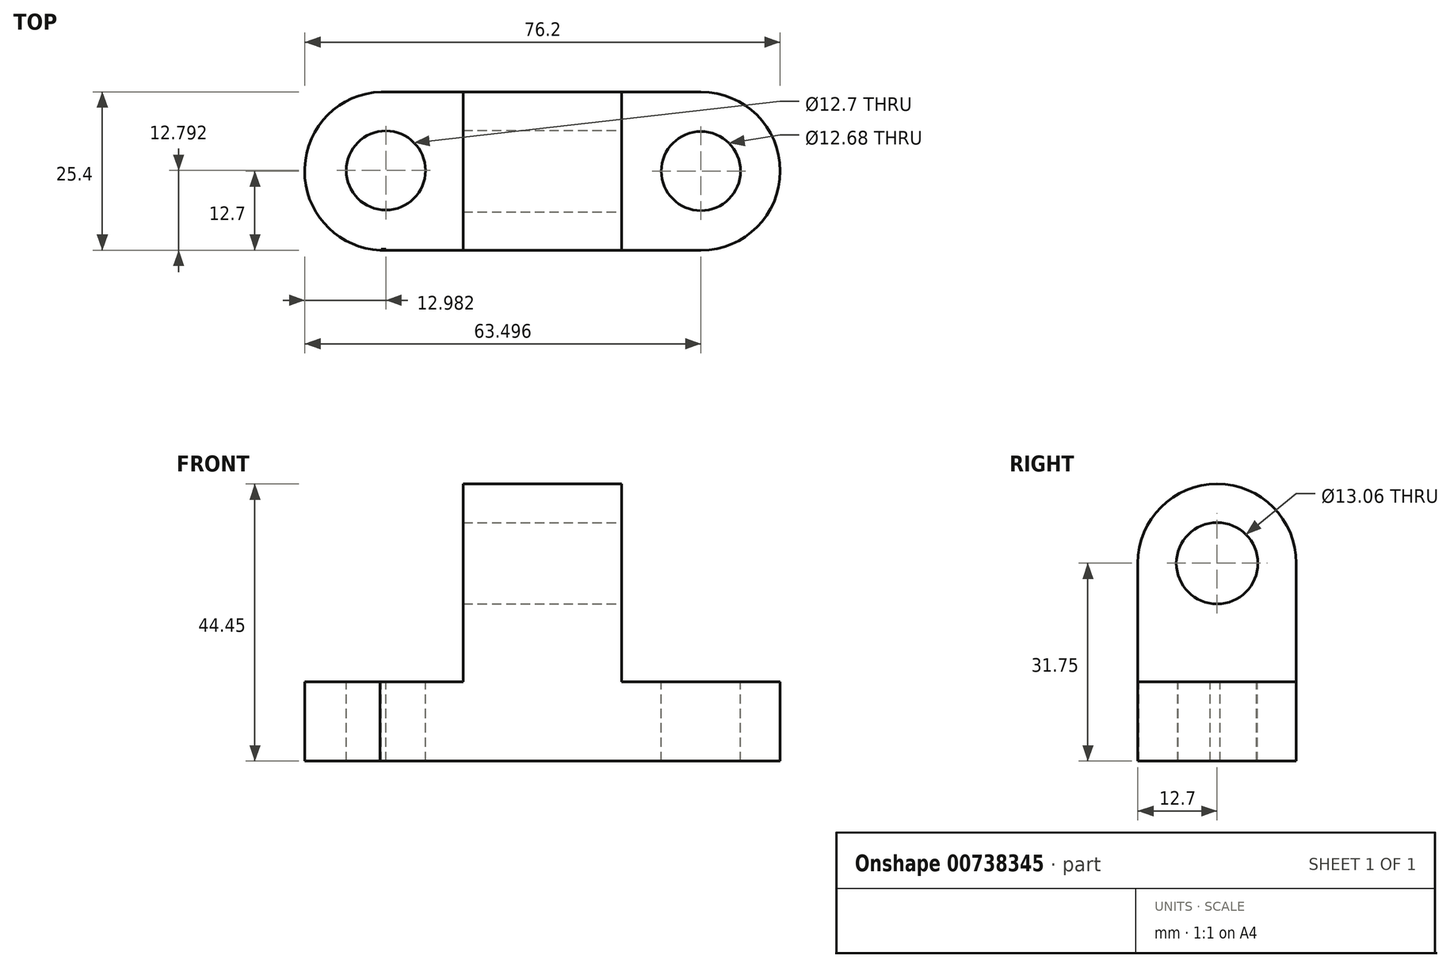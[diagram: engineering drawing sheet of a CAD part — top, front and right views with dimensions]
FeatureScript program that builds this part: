
annotation { "Feature Type Name" : "Feature", "Feature Type Description" : "" }
export const myFeature = defineFeature(function(context is Context, id is Id, definition is map)
    precondition{}
    {
        {
            var Q0;
            Q0=qCreatedBy(makeId("Front.planeOp"),FACE);
            var sketch = newSketch(context, id + "F0", { "sketchPlane" : qUnion([Q0])});
            skLineSegment(sketch, "E0", {"start": v(-38.15, 0) * mm, "end": v(38.05, 0) * mm});
            skLineSegment(sketch, "E1", {"start": v(38.05, 0) * mm, "end": v(38.05, 12.7) * mm});
            skLineSegment(sketch, "E2", {"start": v(38.05, 12.7) * mm, "end": v(12.65, 12.7) * mm});
            skLineSegment(sketch, "E3", {"start": v(12.65, 12.7) * mm, "end": v(12.65, 44.45) * mm});
            skLineSegment(sketch, "E4", {"start": v(12.65, 44.45) * mm, "end": v(-12.75, 44.45) * mm});
            skLineSegment(sketch, "E5", {"start": v(-12.75, 44.45) * mm, "end": v(-12.75, 12.7) * mm});
            skLineSegment(sketch, "E6", {"start": v(-38.15, 0) * mm, "end": v(-38.15, 12.7) * mm});
            skLineSegment(sketch, "E7", {"start": v(-38.15, 12.7) * mm, "end": v(-12.75, 12.7) * mm});
            skSolve(sketch);
        }
        {
            var Q0;
            Q0 = qSketchRegion(id + "F0", true);
            extrude(context, id + "F1", {"entities" : qUnion([Q0]), "depth" : 25.4 * mm, "offsetDistance" : 25.4 * mm});
        }
        {
            var Q0;
            Q0=makeQuery(id+"F1.opExtrude","SWEPT_FACE",FACE,{"disambiguationData":[OSD([sQuery(id+"F0.wireOp",EDGE,"E3")])]});
            var sketch = newSketch(context, id + "F2", { "sketchPlane" : qUnion([Q0])});
            skLineSegment(sketch, "E8", {"start": v(-25.4, 31.75) * mm, "end": v(0, 31.75) * mm});
            skLineSegment(sketch, "E9", {"start": v(0, 31.75) * mm, "end": v(0, 44.45) * mm});
            skArc(sketch, "E10", {"start": v(0, 31.75) * mm, "mid": v(-12.7, 44.45) * mm, "end": v(-25.4, 31.75) * mm});
            skCircle(sketch, "E11", {"center": v(-12.7, 31.75) * mm, "radius": 6.53 * mm});
            skSolve(sketch);
        }
        {
            var Q0;
            {var subQ0=sQuery(id+"F2.wireOp",EDGE,"E11");var subQ1=sQuery(id+"F2.wireOp",EDGE,"E8");var subQ2=makeQuery(id+"F2.imprint","INTERSECT",VERTEX,{"disambiguationData":[OD(0.0)],"derivedFrom":[subQ1,subQ0]});Q0=makeQuery(id+"F2.imprint","IMPRINT",FACE,{"disambiguationData":[TD([[makeQuery(id+"F2.imprint","IMPRINT",EDGE,{"disambiguationData":[TD([[subQ2,-1.0]])],"derivedFrom":subQ1}),1.0]])]});}
            var Q1;
            {var subQ0=sQuery(id+"F2.wireOp",EDGE,"E11");var subQ1=sQuery(id+"F2.wireOp",EDGE,"E8");var subQ2=makeQuery(id+"F2.imprint","INTERSECT",VERTEX,{"disambiguationData":[OD(0.0)],"derivedFrom":[subQ1,subQ0]});Q1=makeQuery(id+"F2.imprint","IMPRINT",FACE,{"disambiguationData":[TD([[makeQuery(id+"F2.imprint","IMPRINT",EDGE,{"disambiguationData":[TD([[subQ2,-1.0]])],"derivedFrom":subQ1}),-1.0]])]});}
            var Q2;
            {var subQ0=sQuery(id+"F2.wireOp",EDGE,"E10");var subQ1=sQuery(id+"F0.wireOp",EDGE,"E3");var subQ2=makeQuery(id+"F1.opExtrude","CAP_EDGE",EDGE,{"disambiguationData":[OSD([subQ1])],"isStart":false});var subQ3=makeQuery(id+"F2.imprint","INTERSECT",VERTEX,{"derivedFrom":[subQ2,sQuery(id+"F2.wireOp",EDGE,"E8"),subQ0]});Q2=makeQuery(id+"F2.imprint","IMPRINT",FACE,{"disambiguationData":[TD([[makeQuery(id+"F2.imprint","IMPRINT",EDGE,{"disambiguationData":[TD([[subQ3,1.0]])],"derivedFrom":subQ0}),-1.0]])]});}
            var Q3;
            {var subQ0=sQuery(id+"F2.wireOp",EDGE,"E9");Q3=makeQuery(id+"F2.imprint","IMPRINT",FACE,{"disambiguationData":[TD([[makeQuery(id+"F2.imprint","IMPRINT",EDGE,{"derivedFrom":subQ0}),1.0]])]});}
            extrude(context, id + "F3", {"entities" : qUnion([Q0, Q1, Q2, Q3]), "operationType" : NewBodyOperationType.REMOVE, "endBound" : BoundingType.THROUGH_ALL, "oppositeDirection" : true, "depth" : 25.4 * mm, "offsetDistance" : 25.4 * mm});
        }
        {
            var Q0;
            Q0=makeQuery(id+"F1.opExtrude","SWEPT_FACE",FACE,{"disambiguationData":[OSD([sQuery(id+"F0.wireOp",EDGE,"E2")])]});
            var sketch = newSketch(context, id + "F4", { "sketchPlane" : qUnion([Q0])});
            skLineSegment(sketch, "E12", {"start": v(25.35, -25.4) * mm, "end": v(25.35, 0) * mm});
            skLineSegment(sketch, "E13", {"start": v(25.35, 0) * mm, "end": v(38.05, 0) * mm});
            skArc(sketch, "E14", {"start": v(25.35, -25.4) * mm, "mid": v(38.05, -12.7) * mm, "end": v(25.35, 0) * mm});
            skLineSegment(sketch, "E15", {"start": v(-25.17, 0) * mm, "end": v(-25.17, -25.22) * mm});
            skLineSegment(sketch, "E16", {"start": v(-25.17, -25.22) * mm, "end": v(-37.87, -25.22) * mm});
            skCircle(sketch, "E17", {"center": v(-25.17, -12.6) * mm, "radius": 6.35 * mm});
            skCircle(sketch, "E18", {"center": v(25.35, -12.7) * mm, "radius": 6.34 * mm});
            skArc(sketch, "E19", {"start": v(-25.17, 0) * mm, "mid": v(-38.16, -12.6) * mm, "end": v(-25.17, -25.22) * mm});
            skSolve(sketch);
        }
        {
            var Q0;
            {var subQ0=sQuery(id+"F4.wireOp",EDGE,"E19");var subQ1=sQuery(id+"F4.wireOp",EDGE,"E16");var subQ3=makeQuery(id+"F4.imprint","INTERSECT",VERTEX,{"derivedFrom":[subQ1,subQ0]});Q0=makeQuery(id+"F4.imprint","IMPRINT",FACE,{"disambiguationData":[TD([[makeQuery(id+"F4.imprint","IMPRINT",EDGE,{"disambiguationData":[TD([[subQ3,1.0]])],"derivedFrom":subQ1}),1.0]])]});}
            var Q1;
            {var subQ0=sQuery(id+"F4.wireOp",EDGE,"E18");var subQ1=sQuery(id+"F4.wireOp",EDGE,"E12");var subQ2=makeQuery(id+"F4.imprint","INTERSECT",VERTEX,{"disambiguationData":[OD(0.0)],"derivedFrom":[subQ1,subQ0]});Q1=makeQuery(id+"F4.imprint","IMPRINT",FACE,{"disambiguationData":[TD([[makeQuery(id+"F4.imprint","IMPRINT",EDGE,{"disambiguationData":[TD([[subQ2,-1.0]])],"derivedFrom":subQ1}),1.0]])]});}
            var Q2;
            {var subQ0=sQuery(id+"F4.wireOp",EDGE,"E18");var subQ1=sQuery(id+"F4.wireOp",EDGE,"E12");var subQ2=makeQuery(id+"F4.imprint","INTERSECT",VERTEX,{"disambiguationData":[OD(0.0)],"derivedFrom":[subQ1,subQ0]});Q2=makeQuery(id+"F4.imprint","IMPRINT",FACE,{"disambiguationData":[TD([[makeQuery(id+"F4.imprint","IMPRINT",EDGE,{"disambiguationData":[TD([[subQ2,-1.0]])],"derivedFrom":subQ1}),-1.0]])]});}
            var Q3;
            {var subQ0=sQuery(id+"F4.wireOp",EDGE,"E17");var subQ1=sQuery(id+"F4.wireOp",EDGE,"E15");var subQ2=makeQuery(id+"F4.imprint","INTERSECT",VERTEX,{"disambiguationData":[OD(0.0)],"derivedFrom":[subQ1,subQ0]});Q3=makeQuery(id+"F4.imprint","IMPRINT",FACE,{"disambiguationData":[TD([[makeQuery(id+"F4.imprint","IMPRINT",EDGE,{"disambiguationData":[TD([[subQ2,-1.0]])],"derivedFrom":subQ1}),-1.0]])]});}
            var Q4;
            {var subQ0=sQuery(id+"F4.wireOp",EDGE,"E17");var subQ1=sQuery(id+"F4.wireOp",EDGE,"E15");var subQ2=makeQuery(id+"F4.imprint","INTERSECT",VERTEX,{"disambiguationData":[OD(0.0)],"derivedFrom":[subQ1,subQ0]});Q4=makeQuery(id+"F4.imprint","IMPRINT",FACE,{"disambiguationData":[TD([[makeQuery(id+"F4.imprint","IMPRINT",EDGE,{"disambiguationData":[TD([[subQ2,-1.0]])],"derivedFrom":subQ1}),1.0]])]});}
            var Q5;
            {var subQ0=sQuery(id+"F4.wireOp",EDGE,"E13");Q5=makeQuery(id+"F4.imprint","IMPRINT",FACE,{"disambiguationData":[TD([[makeQuery(id+"F4.imprint","IMPRINT",EDGE,{"derivedFrom":subQ0}),1.0]])]});}
            var Q6;
            {var subQ0=sQuery(id+"F4.wireOp",EDGE,"E14");var subQ1=sQuery(id+"F0.wireOp",EDGE,"E2");var subQ2=makeQuery(id+"F1.opExtrude","CAP_EDGE",EDGE,{"disambiguationData":[OSD([subQ1])],"isStart":false});var subQ3=makeQuery(id+"F4.imprint","INTERSECT",VERTEX,{"derivedFrom":[subQ2,sQuery(id+"F4.wireOp",EDGE,"E12"),subQ0]});Q6=makeQuery(id+"F4.imprint","IMPRINT",FACE,{"disambiguationData":[TD([[makeQuery(id+"F4.imprint","IMPRINT",EDGE,{"disambiguationData":[TD([[subQ3,-1.0]])],"derivedFrom":subQ0}),-1.0]])]});}
            extrude(context, id + "F5", {"entities" : qUnion([Q0, Q1, Q2, Q3, Q4, Q5, Q6]), "operationType" : NewBodyOperationType.REMOVE, "endBound" : BoundingType.THROUGH_ALL, "oppositeDirection" : true, "depth" : 25.4 * mm, "offsetDistance" : 25.4 * mm});
        }
        {
            var Q0;
            Q0=makeQuery(id+"F1.opExtrude","SWEPT_FACE",FACE,{"disambiguationData":[OSD([sQuery(id+"F0.wireOp",EDGE,"E7")])]});
            var sketch = newSketch(context, id + "F6", { "sketchPlane" : qUnion([Q0])});
            skArc(sketch, "E20", {"start": v(-25.92, 0) * mm, "mid": v(-38.16, -12.6) * mm, "end": v(-25.92, -25.22) * mm});
            skSolve(sketch);
        }
        {
            var Q0;
            Q0 = qSketchRegion(id + "F6", true);
            var Q1;
            {var subQ0=sQuery(id+"F6.wireOp",EDGE,"E20");var subQ1=sQuery(id+"F0.wireOp",EDGE,"E7");var subQ2=makeQuery(id+"F1.opExtrude","CAP_EDGE",EDGE,{"disambiguationData":[OSD([subQ1])],"isStart":true});var subQ3=makeQuery(id+"F6.imprint","INTERSECT",VERTEX,{"derivedFrom":[subQ2,subQ0]});Q1=makeQuery(id+"F6.imprint","IMPRINT",FACE,{"disambiguationData":[TD([[makeQuery(id+"F6.imprint","IMPRINT",EDGE,{"disambiguationData":[TD([[subQ3,-1.0]])],"derivedFrom":subQ0}),-1.0]])]});}
            extrude(context, id + "F7", {"entities" : qUnion([Q0, Q1]), "operationType" : NewBodyOperationType.REMOVE, "endBound" : BoundingType.THROUGH_ALL, "oppositeDirection" : true, "depth" : 25.4 * mm, "offsetDistance" : 25.4 * mm});
        }
        {
            var Q0;
            Q0=makeQuery(id+"F1.opExtrude","SWEPT_FACE",FACE,{"disambiguationData":[OSD([sQuery(id+"F0.wireOp",EDGE,"E7")])]});
            var sketch = newSketch(context, id + "F8", { "sketchPlane" : qUnion([Q0])});
            skLineSegment(sketch, "E21", {"start": v(-26.1, -25.4) * mm, "end": v(-25.92, 0) * mm});
            skArc(sketch, "E22", {"start": v(-25.92, 0) * mm, "mid": v(-38.2, -12.62) * mm, "end": v(-26.1, -25.4) * mm});
            skSolve(sketch);
        }
        {
            var Q0;
            {var subQ0=sQuery(id+"F8.wireOp",EDGE,"E22");var subQ1=makeQuery(id+"F7.boolean.opBoolean","COPY",EDGE,{"derivedFrom":makeQuery(id+"F7.opExtrude","CAP_EDGE",EDGE,{"disambiguationData":[OSD([sQuery(id+"F6.wireOp",EDGE,"E20")])],"isStart":true})});var subQ2=makeQuery(id+"F8.imprint","INTERSECT",VERTEX,{"derivedFrom":[subQ1,subQ0]});Q0=makeQuery(id+"F8.imprint","IMPRINT",FACE,{"disambiguationData":[TD([[makeQuery(id+"F8.imprint","IMPRINT",EDGE,{"disambiguationData":[TD([[subQ2,-1.0]])],"derivedFrom":subQ0}),1.0]])]});}
            var Q1;
            {var subQ0=sQuery(id+"F8.wireOp",EDGE,"E22");var subQ1=sQuery(id+"F0.wireOp",EDGE,"E7");var subQ2=makeQuery(id+"F1.opExtrude","CAP_EDGE",EDGE,{"disambiguationData":[OSD([subQ1])],"isStart":false});var subQ3=makeQuery(id+"F8.imprint","INTERSECT",VERTEX,{"derivedFrom":[subQ2,sQuery(id+"F8.wireOp",EDGE,"E21"),subQ0]});Q1=makeQuery(id+"F8.imprint","IMPRINT",FACE,{"disambiguationData":[TD([[makeQuery(id+"F8.imprint","IMPRINT",EDGE,{"disambiguationData":[TD([[subQ3,1.0]])],"derivedFrom":subQ0}),-1.0]])]});}
            extrude(context, id + "F9", {"entities" : qUnion([Q0, Q1]), "operationType" : NewBodyOperationType.REMOVE, "endBound" : BoundingType.THROUGH_ALL, "oppositeDirection" : true, "depth" : 25.4 * mm, "offsetDistance" : 25.4 * mm});
        }
    });
